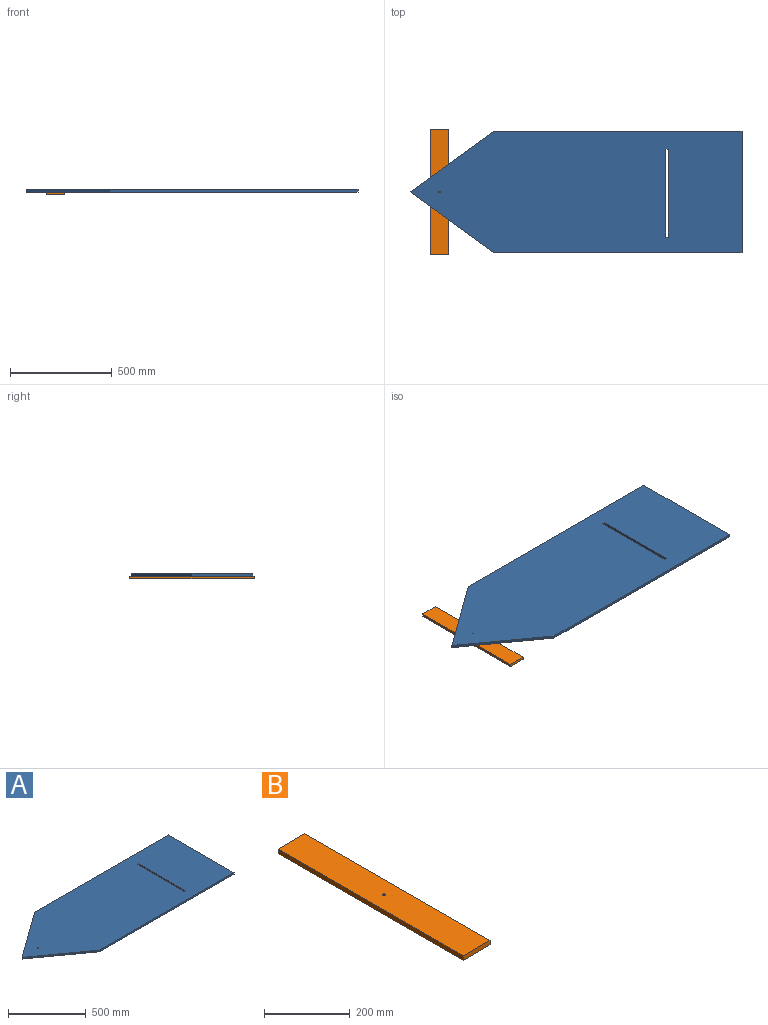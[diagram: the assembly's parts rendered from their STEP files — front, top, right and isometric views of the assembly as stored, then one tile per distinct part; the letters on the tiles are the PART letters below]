
ASSEMBLY  parts=2 mates=1
PART A: 12 faces, bbox 1631x594.8x12.7 mm
  f0: plane 431.8x12.7mm, normal (1,0,0), area 5483.9mm2, adj f1,f9,f10,f11
  f1: plane 12.7x12.45mm, normal (0,-1,0), area 158.1mm2, adj f0,f2,f10,f11
  f2: plane 431.8x12.7mm, normal (-1,0,0), area 5483.9mm2, adj f1,f9,f10,f11
  f3: plane 411.85x297.4mm, normal (-0.59,-0.81,0), area 6451.6mm2, adj f4,f7,f10,f11
  f4: plane 1219.2x12.7mm, normal (0,-1,0), area 15483.8mm2, adj f3,f5,f10,f11
  f5: plane 594.79x12.7mm, normal (1,0,0), area 7553.9mm2, adj f4,f6,f10,f11
  f6: plane 1219.2x12.7mm, normal (0,1,0), area 15483.8mm2, adj f5,f7,f10,f11
  f7: plane 411.85x297.4mm, normal (-0.59,0.81,0), area 6451.6mm2, adj f3,f6,f10,f11
  f8: cylinder r=3.17mm len=12.7mm, axis (0,0,-1), area 253.4mm2, adj f10,f11
  f9: plane 12.7x12.45mm, normal (0,1,0), area 158.1mm2, adj f0,f2,f10,f11
  f10: plane 1631.05x594.79mm, normal (0,0,1), area 842249.4mm2, adj f0,f1,f2,f3,f4,f5,f6,f7
  f11: plane 1631.05x594.79mm, normal (0,0,-1), area 842249.4mm2, adj f0,f1,f2,f3,f4,f5,f6,f7
PART B: 7 faces, bbox 88.9x609.6x12.7 mm
  f0: plane 88.9x12.7mm, normal (0,1,0), area 1129mm2, adj f1,f3,f4,f5
  f1: plane 609.6x12.7mm, normal (-1,0,0), area 7741.9mm2, adj f0,f2,f4,f5
  f2: plane 88.9x12.7mm, normal (0,-1,0), area 1129mm2, adj f1,f3,f4,f5
  f3: plane 609.6x12.7mm, normal (1,0,0), area 7741.9mm2, adj f0,f2,f4,f5
  f4: plane 609.6x88.9mm, normal (0,0,1), area 54161.8mm2, adj f0,f1,f2,f3,f6
  f5: plane 609.6x88.9mm, normal (0,0,-1), area 54161.8mm2, adj f0,f1,f2,f3,f6
  f6: cylinder r=3.17mm len=12.7mm, axis (0,0,1), area 253.4mm2, adj f4,f5
PLACE A t=(156.36,286.85,-303.54)mm
PLACE B t=(-691.54,70.32,-316.24)mm
MATE fastened A.f8 <-> B.f6  axis (0,0,-1) through (-726.3,179.84,-303.54)mm
